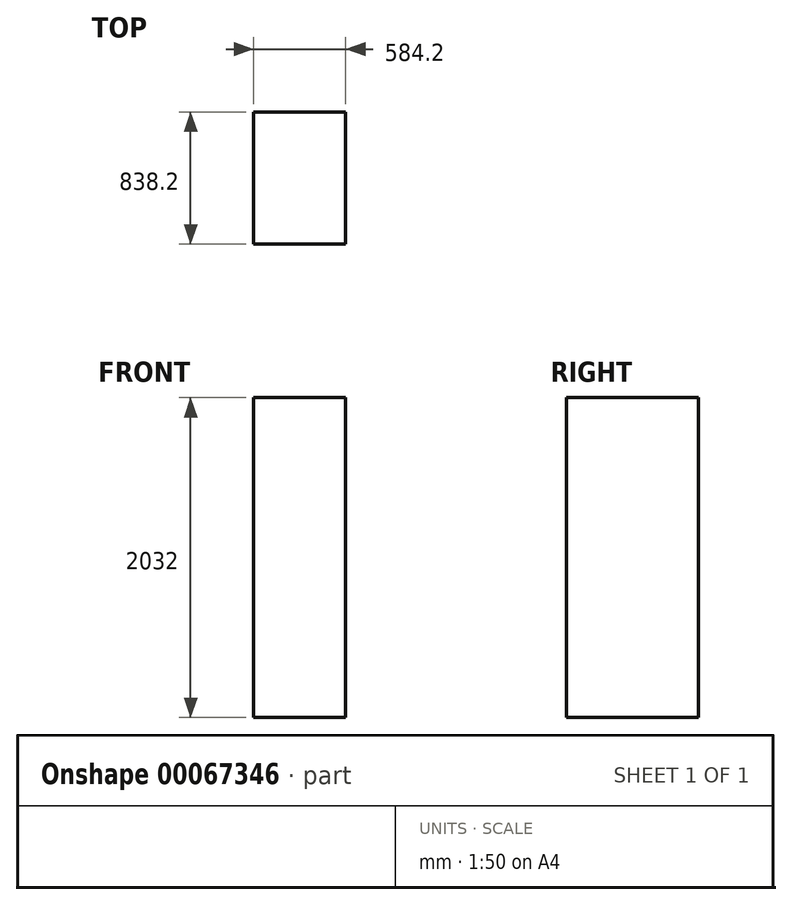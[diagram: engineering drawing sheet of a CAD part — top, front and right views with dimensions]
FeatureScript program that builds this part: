
annotation { "Feature Type Name" : "Feature", "Feature Type Description" : "" }
export const myFeature = defineFeature(function(context is Context, id is Id, definition is map)
    precondition{}
    {
        {
            var Q0;
            Q0=qCreatedBy(makeId("Top.planeOp"),FACE);
            var sketch = newSketch(context, id + "F0", { "sketchPlane" : qUnion([Q0])});
            skLineSegment(sketch, "E0.bottom", {"start": v(292.1, 419.1) * mm, "end": v(-292.1, 419.1) * mm});
            skLineSegment(sketch, "E0.top", {"start": v(292.1, -419.1) * mm, "end": v(-292.1, -419.1) * mm});
            skLineSegment(sketch, "E0.left", {"start": v(292.1, 419.1) * mm, "end": v(292.1, -419.1) * mm});
            skLineSegment(sketch, "E0.right", {"start": v(-292.1, 419.1) * mm, "end": v(-292.1, -419.1) * mm});
            skPoint(sketch, "E0.middle", {"position": v(0, 0) * mm});
            skSolve(sketch);
        }
        {
            var Q0;
            Q0 = qSketchRegion(id + "F0", true);
            extrude(context, id + "F1", {"entities" : qUnion([Q0]), "depth" : 2032 * mm});
        }
    });
